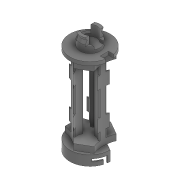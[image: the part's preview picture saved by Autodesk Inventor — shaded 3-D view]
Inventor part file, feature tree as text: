
AUTODESK INVENTOR PART (.ipt)
format: ipt  version: 2022.3 (Build 263350000, 350)  size: 488,448 bytes
history: native  units: mm
features: sketch x18, extrude x16, fillet x2, plane x2, other x1, sweep x1, projected_geometry x1
ambient origin geometry x8: Origin, YZ Plane, XZ Plane, XY Plane, X Axis, Y Axis, Z Axis, Center Point
bodies: Body1 (feature_tree)
feature tree (41):
  other  "Sólido1"
  extrude  "Extrusión1"  Depth=21.0mm
  extrude  "Extrusión2"  Depth=4.6mm
  extrude  "Extrusión3"  Depth=8.0mm TaperAngle=0.0deg
  sweep  "Barrido1"
  extrude  "Extrusión4"  TaperAngle=0.0deg  [1 undecoded]
  extrude  "Extrusión5"  Depth=42.0mm
  extrude  "Extrusión6"  Depth=3.7mm
  extrude  "Extrusión7"  Depth=4.375mm
  extrude  "Extrusión8"  Depth=9.0mm
  fillet  "Empalme1"  Radius=9.0mm
  plane  "Plano de trabajo1"
  extrude  "Extrusión9"  Depth=45.0mm
  plane  "Plano de trabajo2"
  extrude  "Extrusión10"  Depth=3.0mm
  extrude  "Extrusión11"  Depth=3.0mm
  extrude  "Extrusión12"  Depth=68.25mm TaperAngle=0.0deg
  extrude  "Extrusión13"  Depth=8.35mm
  fillet  "Empalme2"  Radius=12.75mm
  extrude  "Extrusión14"  Depth=12.75mm TaperAngle=0.0deg
  extrude  "Extrusión15"  Depth=6.3mm TaperAngle=0.0deg
  extrude  "Extrusión16"  Depth=10.5mm TaperAngle=0.0deg
  sketch  "Boceto1"  dims[d0=21.0mm d1=14.5mm]
  sketch  "Boceto2"  dims[d5=4.6mm d6=8.0mm d7=0.0mm]
  sketch  "Boceto3"  dims[d8=5.0mm d9=5.0mm]
  sketch  "Boceto4"  dims[d10=3.0mm d11=0.0mm d12=0.0mm d13=0.0mm]
  sketch  "Boceto 3D1"  dims[d2=14.0mm d3=0.0mm d4=4.6mm]
  sketch  "Boceto5"  dims[d14=3.0mm d15=0.0mm d16=42.0mm]
  sketch  "Boceto6"  dims[d17=3.7mm d18=0.0mm d19=36.0mm]
  sketch  "Boceto7"  dims[d20=4.375mm d21=4.375mm]
  sketch  "Boceto8"  dims[d22=0.0mm d23=0.0mm d24=9.0mm d25=9.0mm]
  sketch  "Boceto9"  dims[d26=45.0mm d27=45.0mm]
  sketch  "Boceto10"  dims[d28=45.0mm d29=3.0mm]
  sketch  "Boceto11"  dims[d30=3.0mm d31=3.0mm]
  sketch  "Boceto13"  dims[d32=6.3mm d33=0.0mm]
  sketch  "Boceto14"  dims[d34=9.0mm d35=9.0mm d36=45.0mm d37=45.0mm d38=45.0mm d39=3.0mm d40=3.0mm d41=3.0mm d42=68.25mm d43=0.0mm]
  sketch  "Boceto15"  dims[d44=1.0mm d45=8.35mm]
  sketch  "Boceto16"  dims[d46=9.0mm d47=9.0mm d48=45.0mm d49=45.0mm d50=45.0mm d51=3.0mm d52=3.0mm d53=3.0mm d54=12.75mm d55=0.0mm]
  sketch  "Boceto17"  dims[d56=47.25mm]
  sketch  "Boceto18"  dims[d57=9.0mm d58=9.0mm d59=45.0mm d60=45.0mm d61=45.0mm d62=3.0mm d63=3.0mm d64=3.0mm d65=12.75mm d66=0.0mm d67=6.3mm d68=0.0mm d69=10.5mm d70=0.0mm d71=40.0mm d72=14.0mm d73=1.0mm d74=6.8mm d75=0.0mm d76=0.15mm d77=3.0mm d78=6.8mm d79=0.0mm d80=3.0mm d81=1.0mm d82=3.5mm d83=0.0mm d84=0.0mm d85=9.0mm d86=9.0mm d87=2.5mm d88=0.0mm d89=14.25mm d90=4.0mm d91=9.0mm]
  projected_geometry  "Contorno proyectado2"
note: 1 required parameter value undecoded (feature->parameter linkage not recoverable at this tier; creation-order binding heuristic only, values carry confidence <= 0.55)
